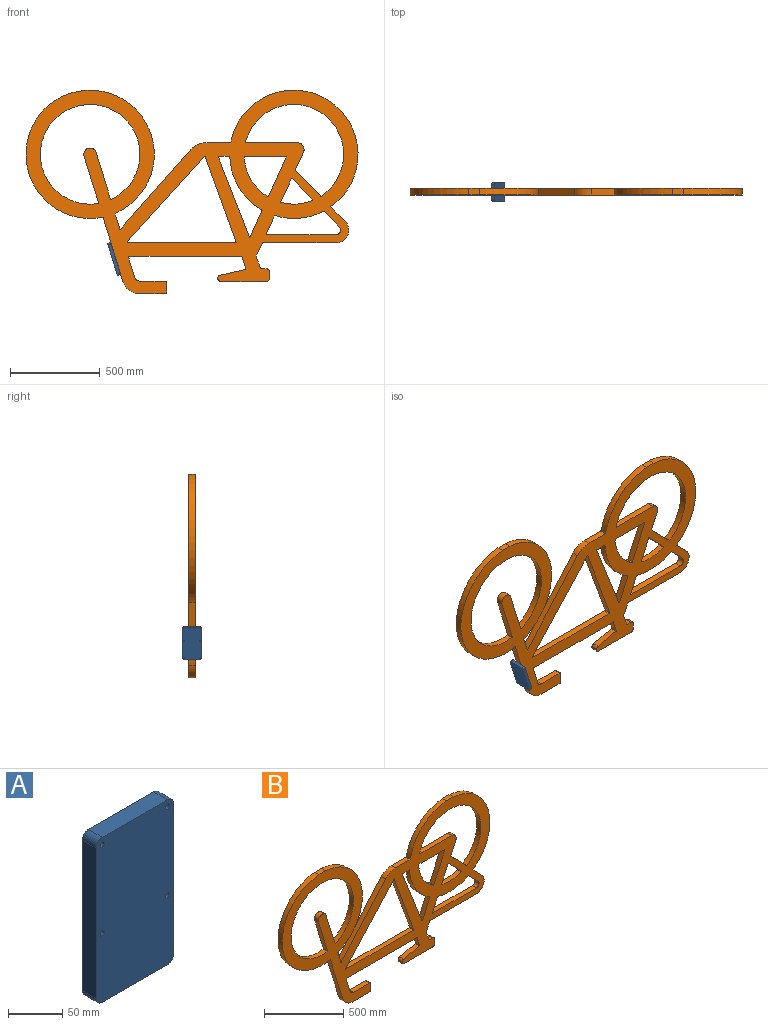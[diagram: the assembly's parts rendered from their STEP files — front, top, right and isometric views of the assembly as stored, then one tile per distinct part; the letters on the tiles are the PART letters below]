
ASSEMBLY  parts=2 mates=1
PART A: 14 faces, bbox 101x18x186 mm
  f0: plane 170x18mm, normal (1,0,0), area 3060mm2, adj f1,f11,f12,f13
  f1: cylinder r=8mm len=18mm, axis (0,1,0), area 226.2mm2, adj f0,f2,f12,f13
  f2: plane 85x18mm, normal (0,0,1), area 1530mm2, adj f1,f3,f12,f13
  f3: cylinder r=8mm len=18mm, axis (0,1,0), area 226.2mm2, adj f2,f4,f12,f13
  f4: plane 170x18mm, normal (-1,0,0), area 3060mm2, adj f3,f5,f12,f13
  f5: cylinder r=8mm len=18mm, axis (0,1,0), area 226.2mm2, adj f4,f6,f12,f13
  f6: plane 85x18mm, normal (0,0,-1), area 1530mm2, adj f5,f11,f12,f13
  f7: cylinder r=3mm len=18mm, axis (0,1,0), area 339.3mm2, adj f12,f13
  f8: cylinder r=3mm len=18mm, axis (0,1,0), area 339.3mm2, adj f12,f13
  f9: cylinder r=3mm len=18mm, axis (0,1,0), area 339.3mm2, adj f12,f13
  f10: cylinder r=3mm len=18mm, axis (0,1,0), area 339.3mm2, adj f12,f13
  f11: cylinder r=8mm len=18mm, axis (0,1,0), area 226.2mm2, adj f0,f6,f12,f13
  f12: plane 186x101mm, normal (0,-1,0), area 18618mm2, adj f0,f1,f2,f3,f4,f5,f6,f7
  f13: plane 186x101mm, normal (0,1,0), area 18618mm2, adj f0,f1,f2,f3,f4,f5,f6,f7
PART B: 93 faces, bbox 1850x36x1132.3 mm
  f0: plane 1850x1132.3mm, normal (0,-1,0), area 657982.5mm2, adj f2,f3,f4,f5,f6,f7,f8,f9
  f1: plane 1850x1132.3mm, normal (0,1,0), area 657982.5mm2, adj f2,f3,f4,f5,f6,f7,f8,f9
  f2: cylinder r=357.5mm len=713.8mm, axis (0,-1,0), area 41873.9mm2, adj f0,f1,f70,f88
  f3: cylinder r=357.5mm len=684.85mm, axis (0,-1,0), area 34162.8mm2, adj f0,f1,f81,f88
  f4: cylinder r=357.5mm len=321.65mm, axis (0,-1,0), area 16687.3mm2, adj f0,f1,f77,f87
  f5: cylinder r=357.5mm len=648.38mm, axis (0,-1,0), area 31467.4mm2, adj f0,f1,f49,f87
  f6: cylinder r=277.5mm len=173.77mm, axis (0,-1,0), area 6376.4mm2, adj f0,f1,f76,f89
  f7: cylinder r=357.5mm len=269.3mm, axis (0,-1,0), area 9983.9mm2, adj f0,f1,f59,f65
  f8: plane 72.03x36mm, normal (0.91,0,-0.42), area 2851.1mm2, adj f0,f1,f60,f80
  f9: plane 96.3x44.01mm, normal (0.91,0,-0.42), area 3811.8mm2, adj f0,f1,f40,f63
  f10: plane 36x27.3mm, normal (0,0,1), area 982.6mm2, adj f0,f1,f56,f90
  f11: plane 252.58x36mm, normal (0,0,-1), area 9092.7mm2, adj f0,f1,f23,f57
  f12: cylinder r=277.5mm len=546.12mm, axis (0,-1,0), area 38770.8mm2, adj f0,f1,f58,f85
  f13: cylinder r=277.5mm len=555mm, axis (0,-1,0), area 59994.2mm2, adj f0,f1,f72,f73
  f14: plane 602.68x36mm, normal (0,0,1), area 21696.3mm2, adj f0,f1,f75,f82
  f15: plane 473.99x172.41mm, normal (-0.94,0,-0.34), area 18157.3mm2, adj f0,f1,f69,f75
  f16: plane 259.75x80.23mm, normal (-0.96,0,-0.3), area 9786.9mm2, adj f0,f1,f17,f73
  f17: cylinder r=35mm len=68.44mm, axis (0,-1,0), area 3958.4mm2, adj f0,f1,f16,f41
  f18: plane 228.51x36mm, normal (0,0,-1), area 8226.4mm2, adj f0,f1,f84,f91
  f19: cylinder r=277.5mm len=222.22mm, axis (0,-1,0), area 9660mm2, adj f0,f1,f84,f92
  f20: plane 129.4x36mm, normal (0,0,1), area 4658.5mm2, adj f0,f1,f43,f77
  f21: plane 100.24x45.81mm, normal (0.91,0,-0.42), area 3967.7mm2, adj f0,f1,f61,f65
  f22: plane 66.59x36mm, normal (0.93,0,0.36), area 2573.4mm2, adj f0,f1,f80,f90
  f23: cylinder r=17.85mm len=36mm, axis (0,-1,0), area 1874.2mm2, adj f0,f1,f11,f24
  f24: plane 140.36x36mm, normal (-0.22,0,0.97), area 5184mm2, adj f0,f1,f23,f83
  f25: plane 67.47x36mm, normal (-0.96,0,-0.3), area 2542mm2, adj f0,f1,f68,f83
  f26: plane 627.15x36mm, normal (0,0,-1), area 22577.2mm2, adj f0,f1,f68,f71
  f27: plane 113.69x36mm, normal (0.96,0,0.3), area 4283.6mm2, adj f0,f1,f28,f71
  f28: cylinder r=29.31mm len=36mm, axis (0,-1,0), area 1341.2mm2, adj f0,f1,f27,f29
  f29: plane 147.68x36mm, normal (0,0,1), area 5316.5mm2, adj f0,f1,f28,f67
  f30: plane 64x36mm, normal (1,0,0), area 2304mm2, adj f0,f1,f64,f67
  f31: plane 147.68x36mm, normal (0,0,-1), area 5316.5mm2, adj f0,f1,f32,f64
  f32: cylinder r=99.31mm len=94.88mm, axis (0,-1,0), area 4544.7mm2, adj f0,f1,f31,f33
  f33: plane 353.15x109.08mm, normal (-0.96,0,-0.3), area 13305.9mm2, adj f0,f1,f32,f70
  f34: plane 82.71x36mm, normal (0.96,0,0.3), area 3116.4mm2, adj f0,f1,f79,f81
  f35: plane 441.3x391.56mm, normal (-0.75,0,0.66), area 21238.9mm2, adj f0,f1,f43,f79
  f36: cylinder r=357.5mm len=296.29mm, axis (0,-1,0), area 13003mm2, adj f0,f1,f66,f74
  f37: plane 57.96x36mm, normal (0,0,-1), area 2086.7mm2, adj f0,f1,f66,f78
  f38: plane 444.2x172.82mm, normal (0.93,0,0.36), area 17158.7mm2, adj f0,f1,f78,f86
  f39: plane 282.79x36mm, normal (0,0,1), area 10180.3mm2, adj f0,f1,f40,f85
  f40: cylinder r=39.82mm len=56.38mm, axis (0,-1,0), area 2866.6mm2, adj f0,f1,f9,f39
  f41: plane 259.75x80.23mm, normal (0.96,0,0.3), area 9786.9mm2, adj f0,f1,f17,f72
  f42: plane 219.82x98.84mm, normal (-0.91,0,0.41), area 8676.6mm2, adj f0,f1,f91,f92
  f43: cylinder r=120.69mm len=90.28mm, axis (0,-1,0), area 3671.7mm2, adj f0,f1,f20,f35
  f44: plane 145.43x65.39mm, normal (-0.91,0,0.41), area 5740.3mm2, adj f0,f1,f74,f86
  f45: plane 127.82x58.42mm, normal (0.91,0,-0.42), area 5059.4mm2, adj f0,f1,f62,f76
  f46: plane 473.99x430.27mm, normal (0.74,0,-0.67), area 23045.4mm2, adj f0,f1,f69,f82
  f47: plane 36x30.97mm, normal (1,0,0), area 1114.8mm2, adj f0,f1,f56,f57
  f48: cylinder r=70mm len=118.79mm, axis (0,1,0), area 5902mm2, adj f0,f1,f49,f53
  f49: plane 82.15x79.85mm, normal (0.72,0,0.7), area 4124.2mm2, adj f0,f1,f5,f48
  f50: plane 87.8x85.35mm, normal (-0.72,0,-0.7), area 4407.9mm2, adj f0,f1,f51,f59
  f51: cylinder r=25mm len=42.43mm, axis (0,1,0), area 2107.8mm2, adj f0,f1,f50,f52
  f52: plane 386.95x36mm, normal (0,0,1), area 13930mm2, adj f0,f1,f51,f61
  f53: plane 410.25x36mm, normal (0,0,-1), area 14769.1mm2, adj f0,f1,f48,f60
  f54: plane 116.73x113.47mm, normal (-0.72,0,-0.7), area 5860.5mm2, adj f0,f1,f62,f89
  f55: plane 141.88x137.93mm, normal (0.72,0,0.7), area 7123.5mm2, adj f0,f1,f58,f63
  f56: cylinder r=20mm len=36mm, axis (0,1,0), area 1131mm2, adj f0,f1,f10,f47
  f57: cylinder r=20mm len=36mm, axis (0,-1,0), area 1131mm2, adj f0,f1,f11,f47
  f58: cylinder r=3mm len=36mm, axis (0,-1,0), area 148.8mm2, adj f0,f1,f12,f55
  f59: cylinder r=3mm len=36mm, axis (0,-1,0), area 138.1mm2, adj f0,f1,f7,f50
  f60: cylinder r=3mm len=36mm, axis (0,-1,0), area 123.3mm2, adj f0,f1,f8,f53
  f61: cylinder r=3mm len=36mm, axis (0,1,0), area 215.9mm2, adj f0,f1,f21,f52
  f62: cylinder r=3mm len=36mm, axis (0,1,0), area 209.7mm2, adj f0,f1,f45,f54
  f63: cylinder r=3mm len=36mm, axis (0,-1,0), area 129.6mm2, adj f0,f1,f9,f55
  f64: cylinder r=3mm len=36mm, axis (0,-1,0), area 169.6mm2, adj f0,f1,f30,f31
  f65: cylinder r=3mm len=36mm, axis (0,-1,0), area 155.4mm2, adj f0,f1,f7,f21
  f66: cylinder r=3mm len=36mm, axis (0,-1,0), area 165.6mm2, adj f0,f1,f36,f37
  f67: cylinder r=3mm len=36mm, axis (0,-1,0), area 169.6mm2, adj f0,f1,f29,f30
  f68: cylinder r=3mm len=36mm, axis (0,1,0), area 137.3mm2, adj f0,f1,f25,f26
  f69: cylinder r=3mm len=36mm, axis (0,1,0), area 222mm2, adj f0,f1,f15,f46
  f70: cylinder r=3mm len=36mm, axis (0,-1,0), area 158.2mm2, adj f0,f1,f2,f33
  f71: cylinder r=3mm len=36mm, axis (0,1,0), area 202mm2, adj f0,f1,f26,f27
  f72: cylinder r=3mm len=36mm, axis (0,-1,0), area 184.6mm2, adj f0,f1,f13,f41
  f73: cylinder r=3mm len=36mm, axis (0,-1,0), area 184.6mm2, adj f0,f1,f13,f16
  f74: cylinder r=3mm len=36mm, axis (0,-1,0), area 158.8mm2, adj f0,f1,f36,f44
  f75: cylinder r=3mm len=36mm, axis (0,1,0), area 207.3mm2, adj f0,f1,f14,f15
  f76: cylinder r=3mm len=36mm, axis (0,-1,0), area 188.4mm2, adj f0,f1,f6,f45
  f77: cylinder r=3mm len=36mm, axis (0,-1,0), area 148.9mm2, adj f0,f1,f4,f20
  f78: cylinder r=3mm len=36mm, axis (0,1,0), area 209.7mm2, adj f0,f1,f37,f38
  f79: cylinder r=3mm len=36mm, axis (0,1,0), area 228.6mm2, adj f0,f1,f34,f35
  f80: cylinder r=3mm len=36mm, axis (0,1,0), area 86.5mm2, adj f0,f1,f8,f22
  f81: cylinder r=3mm len=36mm, axis (0,-1,0), area 158.2mm2, adj f0,f1,f3,f34
  f82: cylinder r=3mm len=36mm, axis (0,1,0), area 249.3mm2, adj f0,f1,f14,f46
  f83: cylinder r=3mm len=36mm, axis (0,1,0), area 177.7mm2, adj f0,f1,f24,f25
  f84: cylinder r=3mm len=36mm, axis (0,-1,0), area 175mm2, adj f0,f1,f18,f19
  f85: cylinder r=3mm len=36mm, axis (0,-1,0), area 197mm2, adj f0,f1,f12,f39
  f86: cylinder r=3mm len=36mm, axis (0,1,0), area 253.6mm2, adj f0,f1,f38,f44
  f87: plane 58.53x36mm, normal (0,0,1), area 2107.2mm2, adj f0,f1,f4,f5
  f88: plane 58.53x36mm, normal (0,0,1), area 2107.2mm2, adj f0,f1,f2,f3
  f89: cylinder r=3mm len=36mm, axis (0,-1,0), area 211.5mm2, adj f0,f1,f6,f54
  f90: cylinder r=3mm len=36mm, axis (0,1,0), area 129.4mm2, adj f0,f1,f10,f22
  f91: cylinder r=3mm len=36mm, axis (0,1,0), area 215.3mm2, adj f0,f1,f18,f42
  f92: cylinder r=3mm len=36mm, axis (0,-1,0), area 183.9mm2, adj f0,f1,f19,f42
PLACE A rot(axis=(-0.7,0.7,-0.11),167.9deg) t=(-543.2,-187.3,-587.47)mm
PLACE B t=(-668.76,-205.27,-1.38)mm
MATE planar A.f12 <-> B.f33  axis (0.96,0,0.3) through (-526.06,-187.3,-581.96)mm
